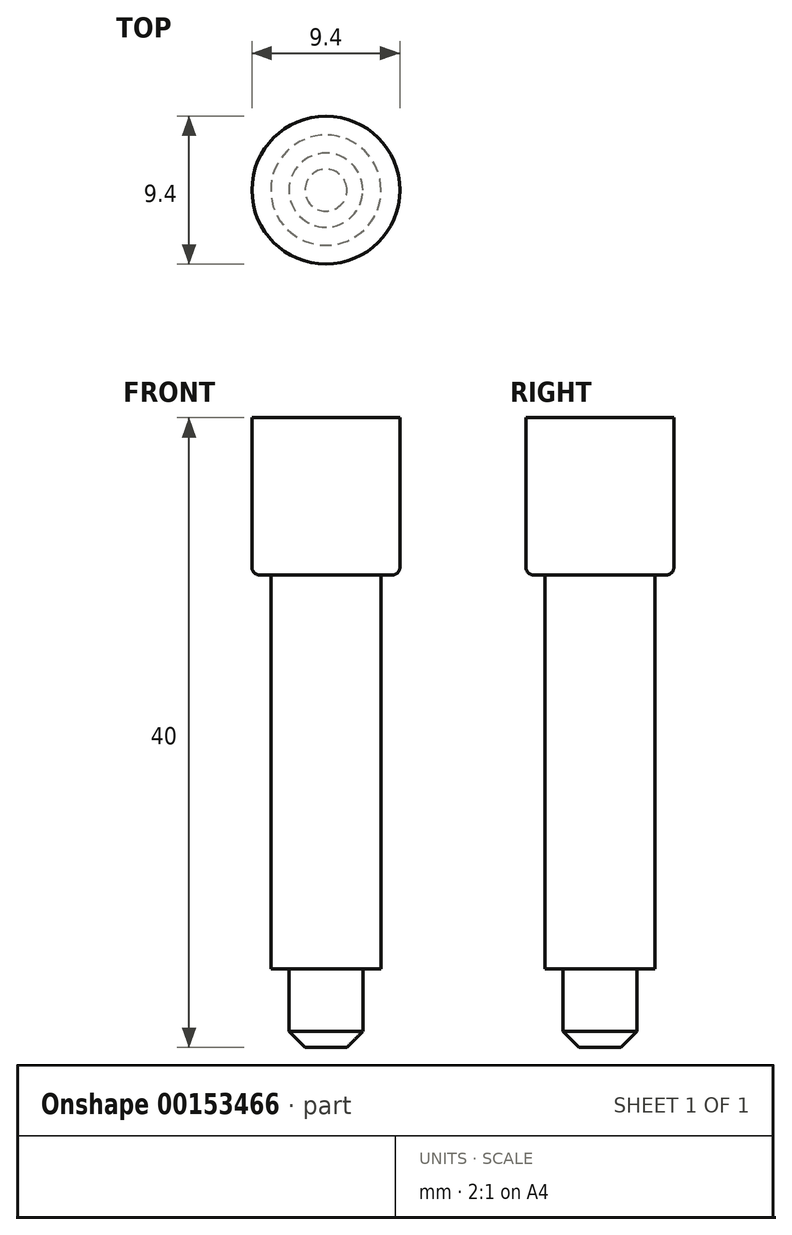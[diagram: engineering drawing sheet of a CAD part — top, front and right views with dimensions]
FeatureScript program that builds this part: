
annotation { "Feature Type Name" : "Feature", "Feature Type Description" : "" }
export const myFeature = defineFeature(function(context is Context, id is Id, definition is map)
    precondition{}
    {
        {
            var Q0;
            Q0=qCreatedBy(makeId("Top.planeOp"),FACE);
            var sketch = newSketch(context, id + "F0", { "sketchPlane" : qUnion([Q0])});
            skCircle(sketch, "E0", {"center": v(0, 0) * mm, "radius": 2.35 * mm});
            skSolve(sketch);
        }
        {
            var Q0;
            Q0 = qSketchRegion(id + "F0", true);
            extrude(context, id + "F1", {"entities" : qUnion([Q0]), "depth" : 5 * mm});
        }
        {
            var Q0;
            Q0=makeQuery(id+"F1.opExtrude","CAP_FACE",FACE,{"disambiguationData":[OSD([sQuery(id+"F0.wireOp",EDGE,"E0")])],"isStart":false});
            var sketch = newSketch(context, id + "F2", { "sketchPlane" : qUnion([Q0])});
            skCircle(sketch, "E1", {"center": v(0, 0) * mm, "radius": 3.5 * mm});
            skSolve(sketch);
        }
        {
            var Q0;
            Q0 = qSketchRegion(id + "F2", true);
            extrude(context, id + "F3", {"entities" : qUnion([Q0]), "operationType" : NewBodyOperationType.ADD, "depth" : 35 * mm});
        }
        {
            var Q0;
            Q0=makeQuery(id+"F1.opExtrude","CAP_EDGE",EDGE,{"disambiguationData":[OSD([sQuery(id+"F0.wireOp",EDGE,"E0")])],"isStart":true});
            chamfer(context, id + "F4", {"entities" : qUnion([Q0]), "width" : 1.02 * mm, "tangentPropagation" : true});
        }
        {
            var Q0;
            Q0=makeQuery(id+"F3.opExtrude","CAP_FACE",FACE,{"disambiguationData":[OSD([sQuery(id+"F2.wireOp",EDGE,"E1")])],"isStart":false});
            var sketch = newSketch(context, id + "F5", { "sketchPlane" : qUnion([Q0])});
            skCircle(sketch, "E2", {"center": v(0, 0) * mm, "radius": 4.7 * mm});
            skSolve(sketch);
        }
        {
            var Q0;
            Q0 = qSketchRegion(id + "F5", true);
            extrude(context, id + "F6", {"entities" : qUnion([Q0]), "operationType" : NewBodyOperationType.ADD, "oppositeDirection" : true, "depth" : 10 * mm});
        }
        {
            var Q0;
            Q0=makeQuery(id+"F6.opExtrude","CAP_EDGE",EDGE,{"disambiguationData":[OSD([sQuery(id+"F5.wireOp",EDGE,"E2")])],"isStart":false});
            fillet(context, id + "F7", {"entities" : qUnion([Q0]), "radius" : .5 * mm, "tangentPropagation" : true, "allowEdgeOverflow" : false});
        }
    });
